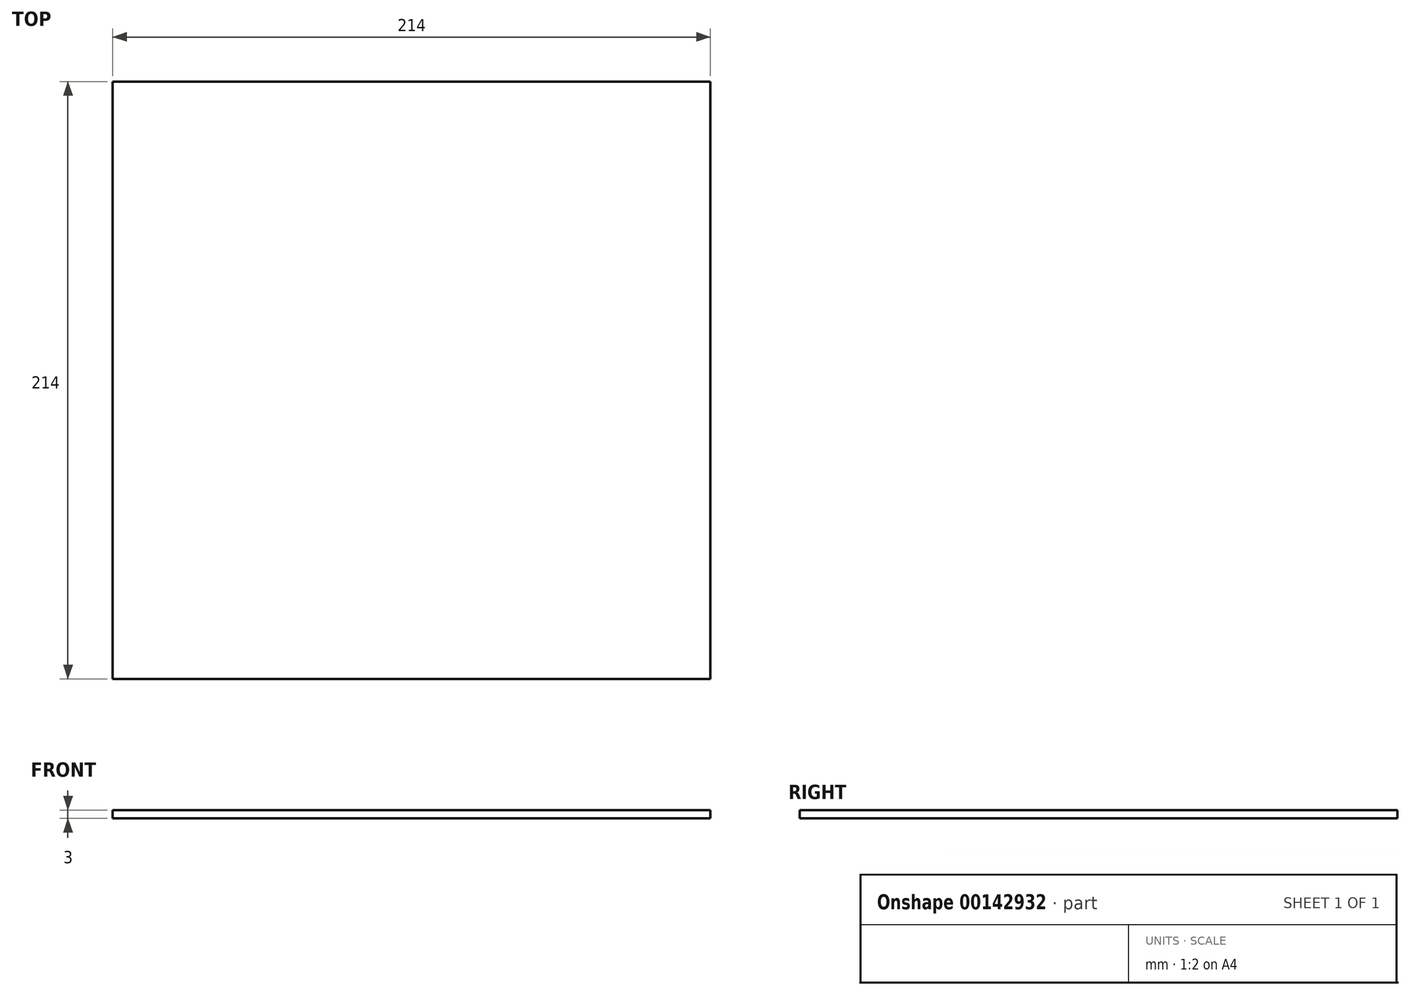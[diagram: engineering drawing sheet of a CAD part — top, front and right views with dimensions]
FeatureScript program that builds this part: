
annotation { "Feature Type Name" : "Feature", "Feature Type Description" : "" }
export const myFeature = defineFeature(function(context is Context, id is Id, definition is map)
    precondition{}
    {
        {
            var Q0;
            Q0=qCreatedBy(makeId("Front.planeOp"),FACE);
            var sketch = newSketch(context, id + "F0", { "sketchPlane" : qUnion([Q0])});
            skLineSegment(sketch, "E0", {"start": v(-107, 0) * mm, "end": v(107, 0) * mm});
            skLineSegment(sketch, "E1.0", {"start": v(-107, 3) * mm, "end": v(107, 3) * mm});
            skLineSegment(sketch, "E2", {"start": v(107, 0) * mm, "end": v(107, 3) * mm});
            skLineSegment(sketch, "E3", {"start": v(-107, 0) * mm, "end": v(-107, 3) * mm});
            skSolve(sketch);
        }
        {
            var Q0;
            Q0 = qSketchRegion(id + "F0", true);
            extrude(context, id + "F1", {"entities" : qUnion([Q0]), "oppositeDirection" : true, "depth" : 214 * mm});
        }
    });
